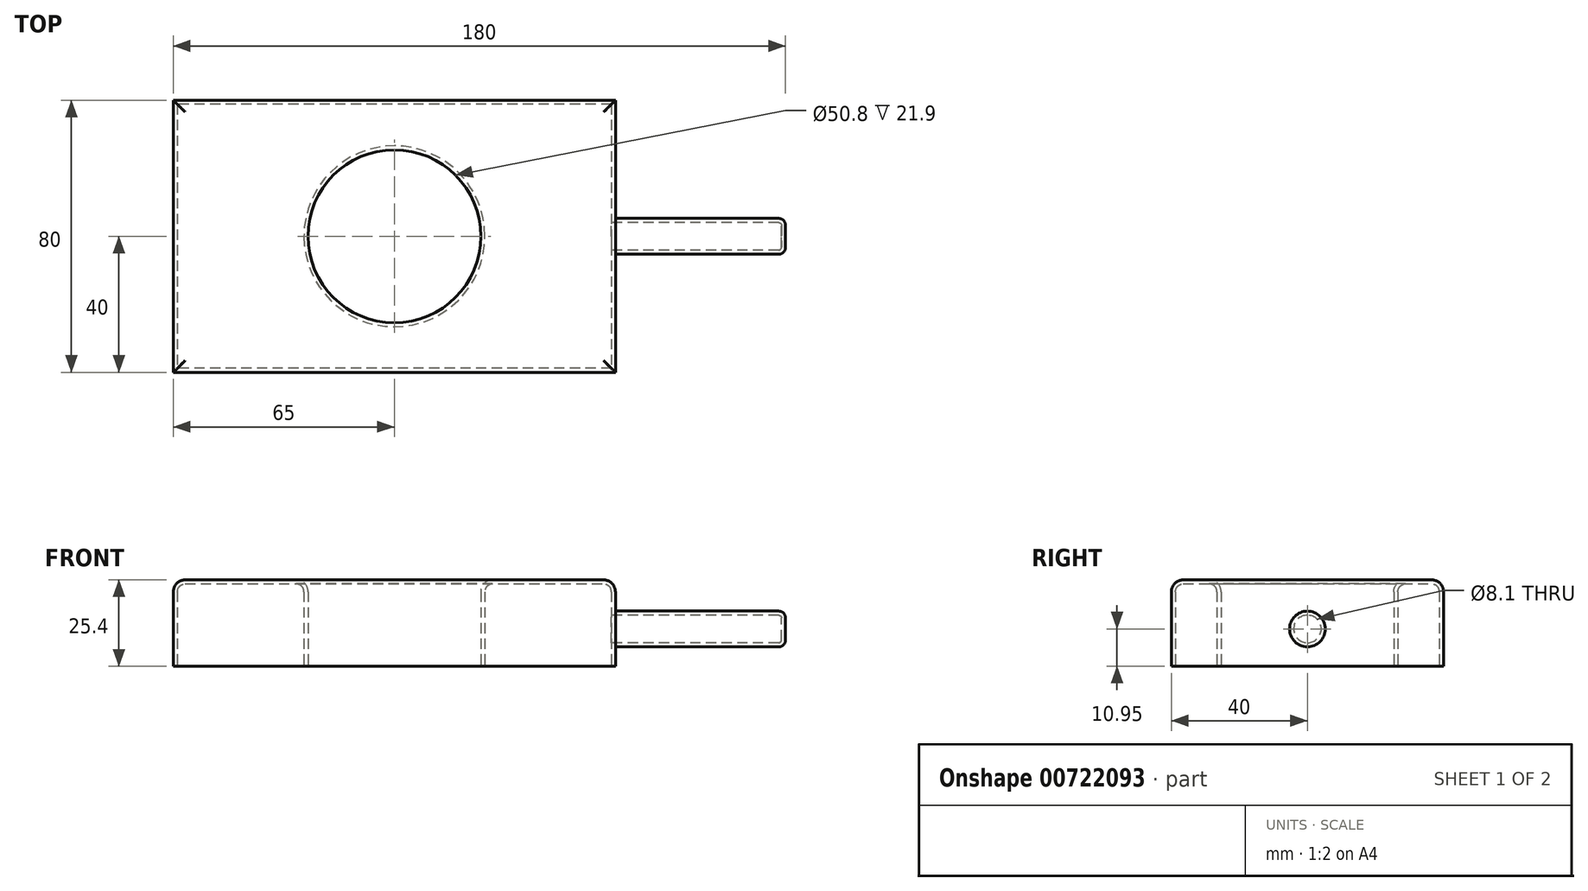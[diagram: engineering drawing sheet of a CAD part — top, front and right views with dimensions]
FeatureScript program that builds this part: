
annotation { "Feature Type Name" : "Feature", "Feature Type Description" : "" }
export const myFeature = defineFeature(function(context is Context, id is Id, definition is map)
    precondition{}
    {
        {
            var Q0;
            Q0=qCreatedBy(makeId("Top.planeOp"),FACE);
            var sketch = newSketch(context, id + "F0", { "sketchPlane" : qUnion([Q0])});
            skLineSegment(sketch, "E0.bottom", {"start": v(65, 40) * mm, "end": v(-65, 40) * mm});
            skLineSegment(sketch, "E0.top", {"start": v(65, -40) * mm, "end": v(-65, -40) * mm});
            skLineSegment(sketch, "E0.left", {"start": v(65, 40) * mm, "end": v(65, -40) * mm});
            skLineSegment(sketch, "E0.right", {"start": v(-65, 40) * mm, "end": v(-65, -40) * mm});
            skPoint(sketch, "E0.middle", {"position": v(0, 0) * mm});
            skCircle(sketch, "E1", {"center": v(0, 0) * mm, "radius": 25.4 * mm});
            skSolve(sketch);
        }
        {
            var Q0;
            Q0 = qSketchRegion(id + "F0", true);
            extrude(context, id + "F1", {"entities" : qUnion([Q0]), "depth" : 25.4 * mm, "offsetDistance" : 25.4 * mm});
        }
        {
            var Q0;
            Q0=makeQuery(id+"F1.opExtrude","CAP_EDGE",EDGE,{"disambiguationData":[OSD([sQuery(id+"F0.wireOp",EDGE,"E0.top")])],"isStart":false});
            var Q1;
            Q1=makeQuery(id+"F1.opExtrude","CAP_EDGE",EDGE,{"disambiguationData":[OSD([sQuery(id+"F0.wireOp",EDGE,"E0.bottom")])],"isStart":false});
            var Q2;
            Q2=makeQuery(id+"F1.opExtrude","CAP_EDGE",EDGE,{"disambiguationData":[OSD([sQuery(id+"F0.wireOp",EDGE,"E0.right")])],"isStart":false});
            var Q3;
            Q3=makeQuery(id+"F1.opExtrude","CAP_EDGE",EDGE,{"disambiguationData":[OSD([sQuery(id+"F0.wireOp",EDGE,"E0.left")])],"isStart":false});
            var Q4;
            Q4=makeQuery(id+"F1.opExtrude","CAP_EDGE",EDGE,{"disambiguationData":[OSD([sQuery(id+"F0.wireOp",EDGE,"E1")])],"isStart":false});
            fillet(context, id + "F2", {"entities" : qUnion([Q0, Q1, Q2, Q3, Q4]), "radius" : 3.5 * mm, "tangentPropagation" : true, "allowEdgeOverflow" : false});
        }
        {
            var Q0;
            Q0=makeQuery(id+"F1.opExtrude","SWEPT_FACE",FACE,{"disambiguationData":[OSD([sQuery(id+"F0.wireOp",EDGE,"E0.left")])]});
            var sketch = newSketch(context, id + "F3", { "sketchPlane" : qUnion([Q0])});
            skCircle(sketch, "E2", {"center": v(0, 10.95) * mm, "radius": 5.25 * mm});
            skPoint(sketch, "E2.centerSnap0", {"position": v(-40, 10.95) * mm});
            skPoint(sketch, "E2.centerSnap1", {"position": v(0, 0) * mm});
            skSolve(sketch);
        }
        {
            var Q0;
            Q0 = qSketchRegion(id + "F3", true);
            extrude(context, id + "F4", {"entities" : qUnion([Q0]), "operationType" : NewBodyOperationType.ADD, "depth" : 50 * mm, "offsetDistance" : 25 * mm});
        }
        {
            var Q0;
            Q0=makeQuery(id+"F4.opExtrude","CAP_EDGE",EDGE,{"disambiguationData":[OSD([sQuery(id+"F3.wireOp",EDGE,"E2")])],"isStart":false});
            fillet(context, id + "F5", {"entities" : qUnion([Q0]), "radius" : 2 * mm, "tangentPropagation" : true, "allowEdgeOverflow" : false});
        }
        {
            var Q0;
            Q0=makeQuery(id+"F1.opExtrude","CAP_FACE",FACE,{"disambiguationData":[OSD([sQuery(id+"F0.wireOp",EDGE,"E0.bottom"),sQuery(id+"F0.wireOp",EDGE,"E0.top"),sQuery(id+"F0.wireOp",EDGE,"E0.left"),sQuery(id+"F0.wireOp",EDGE,"E0.right"),sQuery(id+"F0.wireOp",EDGE,"E1")])],"isStart":true});
            shell(context, id + "F6", {"entities" : qUnion([Q0]), "thickness" : 1.2 * mm});
        }
    });
